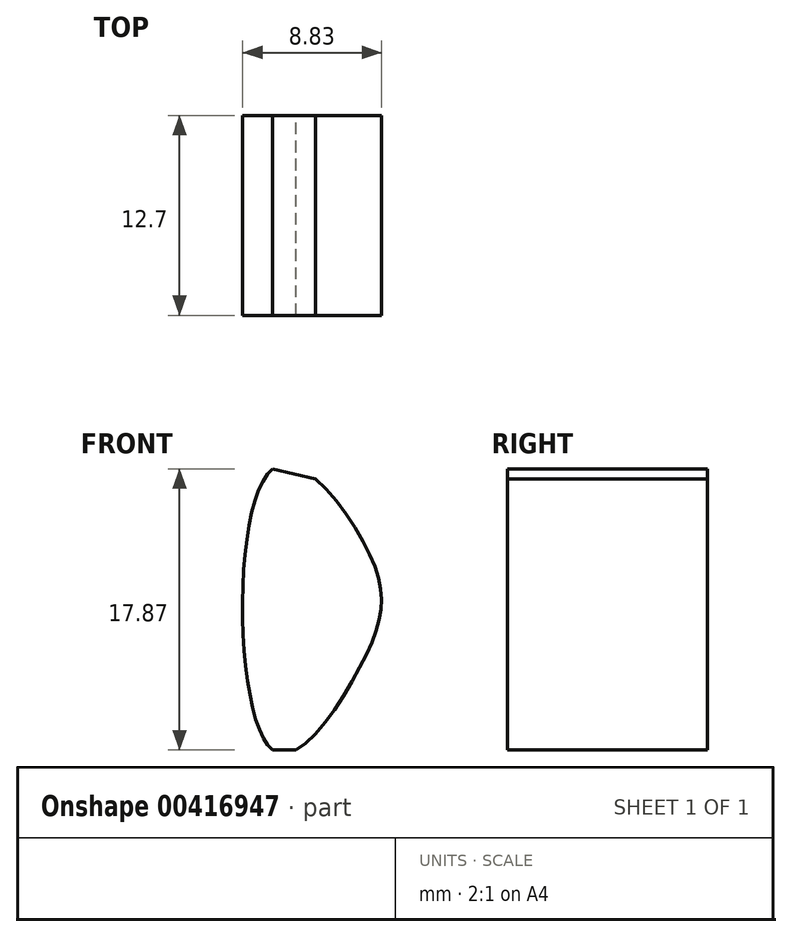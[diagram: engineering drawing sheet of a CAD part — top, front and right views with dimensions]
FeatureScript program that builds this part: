
annotation { "Feature Type Name" : "Feature", "Feature Type Description" : "" }
export const myFeature = defineFeature(function(context is Context, id is Id, definition is map)
    precondition{}
    {
        {
            var Q0;
            Q0=qCreatedBy(makeId("Front.planeOp"),FACE);
            var sketch = newSketch(context, id + "F0", { "sketchPlane" : qUnion([Q0])});
            skLineSegment(sketch, "E0.bottom", {"start": v(-8.08, -20.02) * mm, "end": v(34.66, -20.02) * mm});
            skLineSegment(sketch, "E1", {"start": v(-8.08, -2.15) * mm, "end": v(33.47, -11.89) * mm});
            skFitSpline(sketch, "E2", {"points": [v(-8.08, -2.15) * mm, v(-1.92, -7.58) * mm, v(-2.27, -14.23) * mm, v(-8.08, -20.02) * mm, v(-8.08, -2.15) * mm]});
            skLineSegment(sketch, "E3", {"start": v(34.66, -20.02) * mm, "end": v(47.7, -20.02) * mm});
            skLineSegment(sketch, "E4", {"start": v(47.7, -20.02) * mm, "end": v(33.47, -11.89) * mm});
            skSolve(sketch);
        }
        {
            var Q0;
            {var subQ0=sQuery(id+"F0.wireOp",EDGE,"E1");var subQ1=sQuery(id+"F0.wireOp",EDGE,"E0.bottom");var subQ2=makeQuery(id+"F0.imprint","INTERSECT",VERTEX,{"derivedFrom":[subQ1,subQ0]});Q0=makeQuery(id+"F0.imprint","IMPRINT",FACE,{"disambiguationData":[TD([[makeQuery(id+"F0.imprint","IMPRINT",EDGE,{"disambiguationData":[TD([[subQ2,1.0]])],"derivedFrom":subQ1}),1.0]])]});}
            extrude(context, id + "F1", {"entities" : qUnion([Q0]), "endBound" : BoundingType.SYMMETRIC, "depth" : 12.7 * mm, "offsetDistance" : 25.4 * mm});
        }
    });
